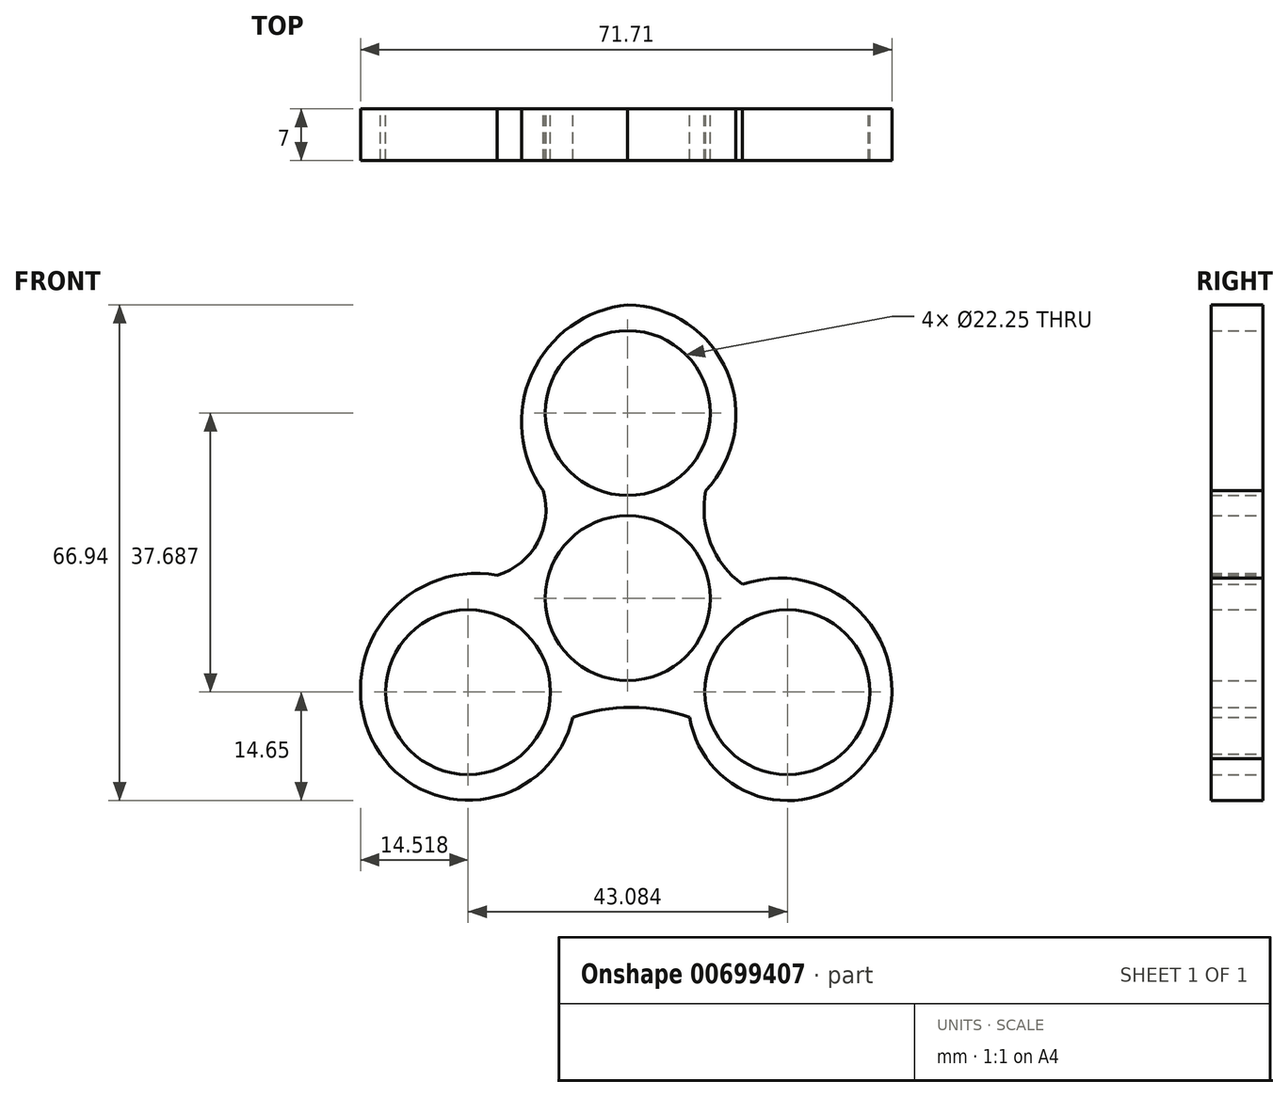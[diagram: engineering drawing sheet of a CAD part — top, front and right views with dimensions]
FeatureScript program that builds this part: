
annotation { "Feature Type Name" : "Feature", "Feature Type Description" : "" }
export const myFeature = defineFeature(function(context is Context, id is Id, definition is map)
    precondition{}
    {
        {
            var Q0;
            Q0=qCreatedBy(makeId("Front.planeOp"),FACE);
            var sketch = newSketch(context, id + "F0", { "sketchPlane" : qUnion([Q0])});
            skCircle(sketch, "E0", {"center": v(0, 37.69) * mm, "radius": 11.12 * mm});
            skCircle(sketch, "E1", {"center": v(0, 12.69) * mm, "radius": 11.12 * mm});
            skCircle(sketch, "E2", {"center": v(21.54, 0) * mm, "radius": 11.12 * mm});
            skCircle(sketch, "E3", {"center": v(-21.54, 0) * mm, "radius": 11.12 * mm});
            skArc(sketch, "E4", {"start": v(-17.61, 15.78) * mm, "mid": v(-12.15, 20.22) * mm, "end": v(-11.43, 27.23) * mm});
            skArc(sketch, "E5", {"start": v(0, 52.3) * mm, "mid": v(-12.91, 43.04) * mm, "end": v(-11.43, 27.23) * mm});
            skArc(sketch, "E6", {"start": v(10.54, 27.23) * mm, "mid": v(13.43, 43.2) * mm, "end": v(0, 52.3) * mm});
            skArc(sketch, "E7", {"start": v(10.54, 27.23) * mm, "mid": v(11.16, 20.16) * mm, "end": v(15.5, 14.54) * mm});
            skArc(sketch, "E8", {"start": v(32.51, -8.97) * mm, "mid": v(32.77, 9.13) * mm, "end": v(15.5, 14.54) * mm});
            skArc(sketch, "E9", {"start": v(8.38, -3.4) * mm, "mid": v(18.57, -14.3) * mm, "end": v(32.51, -8.97) * mm});
            skArc(sketch, "E10", {"start": v(8.38, -3.4) * mm, "mid": v(0.49, -2.04) * mm, "end": v(-7.4, -3.4) * mm});
            skArc(sketch, "E11", {"start": v(-33.4, -8.35) * mm, "mid": v(-18.79, -14.34) * mm, "end": v(-7.4, -3.4) * mm});
            skArc(sketch, "E12", {"start": v(-17.61, 15.78) * mm, "mid": v(-33.5, 8.94) * mm, "end": v(-33.4, -8.35) * mm});
            skSolve(sketch);
        }
        {
            var Q0;
            Q0=makeQuery(id+"F0.imprint","IMPRINT",FACE,{"disambiguationData":[TD([[makeQuery(id+"F0.imprint","IMPRINT",EDGE,{"derivedFrom":sQuery(id+"F0.wireOp",EDGE,"E0")}),-1.0]])]});
            extrude(context, id + "F1", {"entities" : qUnion([Q0]), "depth" : 7 * mm, "offsetDistance" : 25 * mm});
        }
    });
